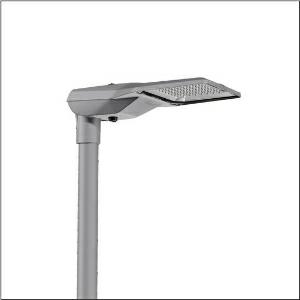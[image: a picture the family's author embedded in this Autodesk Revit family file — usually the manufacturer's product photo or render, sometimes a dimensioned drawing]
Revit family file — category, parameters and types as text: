
# Revit family: streetlight_sl_21_midi___p0_8a_5xe3u33t08nb_6486
name_source: partatom
category: Lighting Fixtures
units: mm (PartAtom-declared; Revit-internal decimal feet)

## family parameters
Cut with Voids When Loaded = No
Host = Face
Light Source = No
Part Type = Normal
Room Calculation Point = No
Round Connector Dimension = Use Diameter
Shared = No

## types (1)
- --- (1 x LED, 22900 lm, 151.2 W, 3000K)
    Apparent Load = 151 VA
    CIE Flux Codes = 36 69 97 100 100
    Color Rendering = 70
    Color Temperature = 3000K
    Default Elevation = 1800 mm
    Description = Streetlight SL 21 midi, mast luminaire, primary light control with lens, of PMMA, primary optical cover: cover, of toughened safety glass, transparent, light distribution: P0.8a, light emission: direct distribution, primary light characteristic: asymmetric, installation type: post-top, side-entry, LED, High Power LED, rated luminous flux: 22.900lm, luminous efficacy: 152lm/W, light colour: 730, colour temperature: 3000K, control gear: D4i, control: pre-setting: logarithmic dimming characteristic, flexible luminous flux parameterisation, time-dependent luminous flux control, constant luminous flux control, overheat protection, mains connection: 230..240V, AC, 50/60Hz, start of lifetime: 151W, end of service life: 157W, reduction: 70W, luminaire housing, of diecast aluminium, powder-coated, SITECO metallic grey (DB 702S), corrosivity category C5 high according to DIN EN ISO 12944, multi-level sealing system, sealing non-destructively replaceable, inclination adjustable: 0°, 5°, 10°, 15°, please order mast flange separately, length: 644mm, width: 335mm, height: 110mm, mast flange for spigot size: 42mm (side-entry): 5XC10008XM4, 60/48mm (side-entry/post-top): 5XC10108XM2, 76/60mm (side-entry/post-top): 5XC10108XM1, mounting height: 4..8m, Smart Interface below and above, protection rating (complete): IP66, insulation class (complete): insulation class II (safety insulation), certification: CE, ENEC, ENEC+, VDE, impact resistance: IK10, permissible operating ambient temperature for outdoor applications: -40..+50°C, standard-compliant lighting for roads and squares, packaging unit: 1 piece

Light Distribution: P0.8a
    Height = 111 mm
    Lamp = 1 x LED
    Lamp Light Flux = 22900 lm
    Lamp Power = 151.2 W
    Lamp count = 1
    Length = 644 mm
    Luminous efficacy = 151 lm/W
    Manufacturer = Siteco
    ModVariant = No
    Model = 5XE3U33T08NB
    Number of Poles = 1
    OnlyDefault = Yes
    Power Factor = 1
    Product Name = Streetlight SL 21 midi | P0.8a
    Product group = mast luminaire | pylon top
    ProductGroupID = 6100
    Protection Class = Protection class II
    Protection Degree = IP 66
    RLX_Detail_Level = 1
    RLX_Emergency_Light_Flux = 0 lm
    RLX_Emergency_Type = 0
    RLX_Emergency_Type_DB = No
    RlxData = <blob elided: 90841 chars, md5=1a276f3e>
    Socket = socket
    Standby Power = 0 W
    System Light Flux = 22901 lm
    System Power = 151 W
    Type Comments = factory setting: luminous flux: 100 % | dim-lin: 254 | 802 mA
    Type Image = l_1004304.jpg
    URL = http://relux.com
    VarID = @adj_079143
    Voltage = 0 V
    Weight = 0.00 kg
    Width = 336 mm

## geometry (parser evidence)
native form markers: Blend x4, Sweep x12
no freeform markers — native parametric forms only
